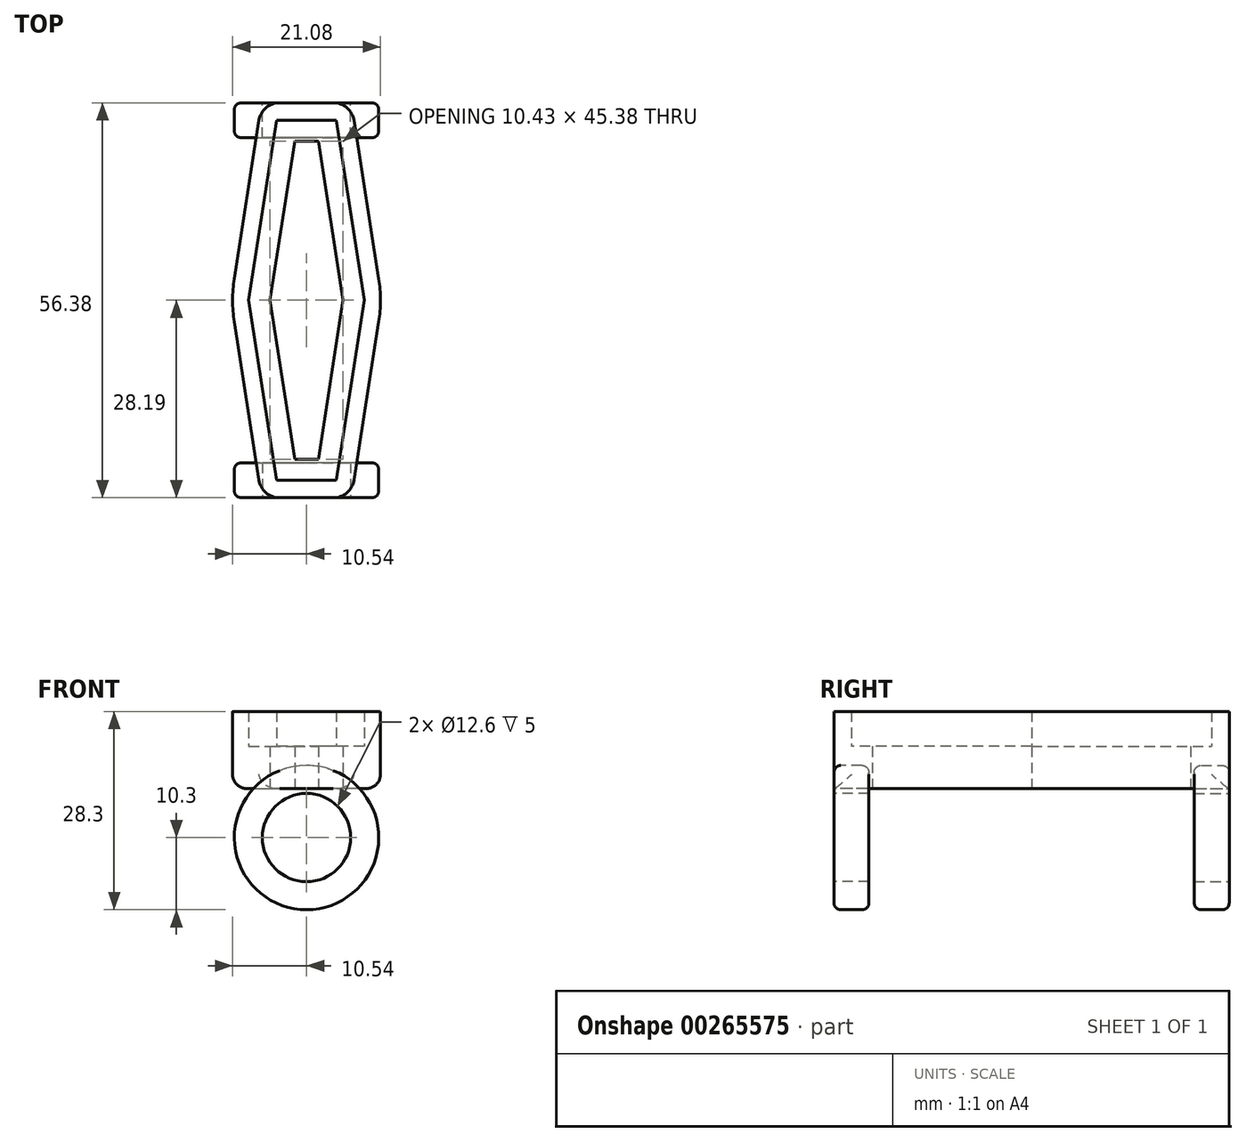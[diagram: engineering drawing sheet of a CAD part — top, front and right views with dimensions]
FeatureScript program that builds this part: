
annotation { "Feature Type Name" : "Feature", "Feature Type Description" : "" }
export const myFeature = defineFeature(function(context is Context, id is Id, definition is map)
    precondition{}
    {
        {
            var Q0;
            Q0=qCreatedBy(makeId("Top.planeOp"),FACE);
            var sketch = newSketch(context, id + "F0", { "sketchPlane" : qUnion([Q0])});
            skLineSegment(sketch, "E0", {"start": v(0, 0) * mm, "end": v(8.25, 0) * mm, "construction": true});
            skLineSegment(sketch, "E1", {"start": v(8.25, 0) * mm, "end": v(4.25, 25.7) * mm});
            skLineSegment(sketch, "E2", {"start": v(0, 0) * mm, "end": v(0, 25.46) * mm, "construction": true});
            skLineSegment(sketch, "E3", {"start": v(4.25, 25.7) * mm, "end": v(0, 25.7) * mm});
            skLineSegment(sketch, "E4.MirrorCS", {"start": v(-4.25, 25.7) * mm, "end": v(0, 25.7) * mm});
            skLineSegment(sketch, "E5.MirrorCS", {"start": v(-8.25, 0) * mm, "end": v(-4.25, 25.7) * mm});
            skLineSegment(sketch, "E6.MirrorCS", {"start": v(0, 0) * mm, "end": v(-8.25, 0) * mm, "construction": true});
            skLineSegment(sketch, "E7.MirrorCS", {"start": v(-8.25, 0) * mm, "end": v(-4.25, -25.7) * mm});
            skLineSegment(sketch, "E8.MirrorCS", {"start": v(-4.25, -25.7) * mm, "end": v(0, -25.7) * mm});
            skLineSegment(sketch, "E9.MirrorCS", {"start": v(4.25, -25.7) * mm, "end": v(0, -25.7) * mm});
            skLineSegment(sketch, "E10.MirrorCS", {"start": v(8.25, 0) * mm, "end": v(4.25, -25.7) * mm});
            skLineSegment(sketch, "E11.0", {"start": v(4.25, 22.7) * mm, "end": v(0, 22.7) * mm});
            skLineSegment(sketch, "E11.1", {"start": v(-4.25, 22.7) * mm, "end": v(0, 22.7) * mm});
            skLineSegment(sketch, "E12.MirrorCS", {"start": v(-4.25, -22.7) * mm, "end": v(0, -22.7) * mm});
            skLineSegment(sketch, "E13.MirrorCS", {"start": v(4.25, -22.7) * mm, "end": v(0, -22.7) * mm});
            skLineSegment(sketch, "E14.0", {"start": v(-10.78, 0) * mm, "end": v(-6.4, -28.2) * mm});
            skLineSegment(sketch, "E14.1", {"start": v(-6.4, -28.2) * mm, "end": v(0, -28.2) * mm});
            skLineSegment(sketch, "E14.2", {"start": v(-10.78, 0) * mm, "end": v(-6.4, 28.2) * mm});
            skLineSegment(sketch, "E14.3", {"start": v(6.4, -28.2) * mm, "end": v(0, -28.2) * mm});
            skLineSegment(sketch, "E14.4", {"start": v(-6.4, 28.2) * mm, "end": v(0, 28.2) * mm});
            skLineSegment(sketch, "E14.5", {"start": v(6.4, 28.2) * mm, "end": v(0, 28.2) * mm});
            skLineSegment(sketch, "E14.6", {"start": v(10.78, 0) * mm, "end": v(6.4, 28.2) * mm});
            skLineSegment(sketch, "E14.7", {"start": v(10.78, 0) * mm, "end": v(6.4, -28.2) * mm});
            skLineSegment(sketch, "E15.0", {"start": v(-5.21, 0) * mm, "end": v(-1.68, -22.7) * mm});
            skLineSegment(sketch, "E15.1", {"start": v(-1.68, -22.7) * mm, "end": v(0, -22.7) * mm});
            skLineSegment(sketch, "E15.2", {"start": v(-5.21, 0) * mm, "end": v(-1.68, 22.7) * mm});
            skLineSegment(sketch, "E15.3", {"start": v(1.68, -22.7) * mm, "end": v(0, -22.7) * mm});
            skLineSegment(sketch, "E15.4", {"start": v(-1.68, 22.7) * mm, "end": v(0, 22.7) * mm});
            skLineSegment(sketch, "E15.5", {"start": v(1.68, 22.7) * mm, "end": v(0, 22.7) * mm});
            skLineSegment(sketch, "E15.6", {"start": v(5.21, 0) * mm, "end": v(1.68, 22.7) * mm});
            skLineSegment(sketch, "E15.7", {"start": v(5.21, 0) * mm, "end": v(1.68, -22.7) * mm});
            skSolve(sketch);
        }
        {
            var Q0;
            {var subQ9=sQuery(id+"F0.wireOp",EDGE,"E5.MirrorCS");Q0=makeQuery(id+"F0.imprint","IMPRINT",FACE,{"disambiguationData":[TD([[makeQuery(id+"F0.imprint","IMPRINT",EDGE,{"derivedFrom":subQ9}),-1.0]])]});}
            var Q1;
            {var subQ3=sQuery(id+"F0.wireOp",EDGE,"E3");var subQ8=sQuery(id+"F0.wireOp",EDGE,"E4.MirrorCS");var subQ10=makeQuery(id+"F0.imprint","INTERSECT",VERTEX,{"derivedFrom":[subQ3,subQ8]});Q1=makeQuery(id+"F0.imprint","IMPRINT",FACE,{"disambiguationData":[TD([[makeQuery(id+"F0.imprint","IMPRINT",EDGE,{"disambiguationData":[TD([[subQ10,1.0]])],"derivedFrom":subQ3}),1.0]])]});}
            var Q2;
            {var subQ5=sQuery(id+"F0.wireOp",EDGE,"E1");Q2=makeQuery(id+"F0.imprint","IMPRINT",FACE,{"disambiguationData":[TD([[makeQuery(id+"F0.imprint","IMPRINT",EDGE,{"derivedFrom":subQ5}),1.0]])]});}
            var Q3;
            {var subQ3=sQuery(id+"F0.wireOp",EDGE,"E9.MirrorCS");var subQ5=sQuery(id+"F0.wireOp",EDGE,"E8.MirrorCS");var subQ6=makeQuery(id+"F0.imprint","INTERSECT",VERTEX,{"derivedFrom":[subQ5,subQ3]});Q3=makeQuery(id+"F0.imprint","IMPRINT",FACE,{"disambiguationData":[TD([[makeQuery(id+"F0.imprint","IMPRINT",EDGE,{"disambiguationData":[TD([[subQ6,1.0]])],"derivedFrom":subQ5}),1.0]])]});}
            extrude(context, id + "F1", {"entities" : qUnion([Q0, Q1, Q2, Q3]), "depth" : 6 * mm});
        }
        {
            var Q0;
            Q0 = qSketchRegion(id + "F0", true);
            extrude(context, id + "F2", {"entities" : qUnion([Q0]), "operationType" : NewBodyOperationType.ADD, "depth" : 11 * mm});
        }
        {
            var Q0;
            Q0=makeQuery(id+"F2.opExtrude","SWEPT_FACE",FACE,{"disambiguationData":[OSD([sQuery(id+"F0.wireOp",EDGE,"E14.1"),sQuery(id+"F0.wireOp",EDGE,"E14.3")])]});
            var sketch = newSketch(context, id + "F3", { "sketchPlane" : qUnion([Q0])});
            skLineSegment(sketch, "E16", {"start": v(0, 0) * mm, "end": v(0, -7) * mm});
            skCircle(sketch, "E17", {"center": v(0, -7) * mm, "radius": 6.3 * mm});
            skCircle(sketch, "E18.0", {"center": v(0, -7) * mm, "radius": 10.3 * mm});
            skSolve(sketch);
        }
        {
            var Q0;
            Q0 = qSketchRegion(id + "F3", true);
            extrude(context, id + "F4", {"entities" : qUnion([Q0]), "oppositeDirection" : true, "depth" : 5 * mm});
        }
        {
            var Q0;
            {var subQ0=sQuery(id+"F0.wireOp",EDGE,"E10.MirrorCS");var subQ1=sQuery(id+"F0.wireOp",EDGE,"E9.MirrorCS");var subQ2=sQuery(id+"F0.wireOp",EDGE,"E8.MirrorCS");var subQ3=sQuery(id+"F0.wireOp",EDGE,"E7.MirrorCS");var subQ4=sQuery(id+"F0.wireOp",EDGE,"E5.MirrorCS");var subQ5=sQuery(id+"F0.wireOp",EDGE,"E4.MirrorCS");var subQ6=sQuery(id+"F0.wireOp",EDGE,"E3");var subQ7=sQuery(id+"F0.wireOp",EDGE,"E1");Q0=makeQuery(id+"F2.boolean.opBoolean","MERGE",FACE,{"derivedFrom":[makeQuery(id+"F1.opExtrude","CAP_FACE",FACE,{"disambiguationData":[OSD([subQ7,subQ6,subQ5,subQ4,subQ3,subQ2,subQ1,subQ0,sQuery(id+"F0.wireOp",EDGE,"E15.0"),sQuery(id+"F0.wireOp",EDGE,"E15.1"),sQuery(id+"F0.wireOp",EDGE,"E15.2"),sQuery(id+"F0.wireOp",EDGE,"E15.3"),sQuery(id+"F0.wireOp",EDGE,"E15.4"),sQuery(id+"F0.wireOp",EDGE,"E15.5"),sQuery(id+"F0.wireOp",EDGE,"E15.6"),sQuery(id+"F0.wireOp",EDGE,"E15.7")])],"isStart":true}),makeQuery(id+"F2.opExtrude","CAP_FACE",FACE,{"disambiguationData":[OSD([subQ7,subQ6,subQ5,subQ4,subQ3,subQ2,subQ1,subQ0,sQuery(id+"F0.wireOp",EDGE,"E14.0"),sQuery(id+"F0.wireOp",EDGE,"E14.1"),sQuery(id+"F0.wireOp",EDGE,"E14.2"),sQuery(id+"F0.wireOp",EDGE,"E14.3"),sQuery(id+"F0.wireOp",EDGE,"E14.4"),sQuery(id+"F0.wireOp",EDGE,"E14.5"),sQuery(id+"F0.wireOp",EDGE,"E14.6"),sQuery(id+"F0.wireOp",EDGE,"E14.7")])],"isStart":true})]});}
            var sketch = newSketch(context, id + "F5", { "sketchPlane" : qUnion([Q0])});
            skLineSegment(sketch, "E19", {"start": v(10.78, 0) * mm, "end": v(-10.78, 0) * mm});
            skSolve(sketch);
        }
        {
            var Q0;
            Q0=sQuery(id+"F5.wireOp",EDGE,"E19");
            extrude(context, id + "F6", {"bodyType" : ToolBodyType.SURFACE, "surfaceEntities" : qUnion([Q0]), "depth" : 25 * mm});
        }
        {
            var Q0;
            Q0=makeQuery(id+"F4.opExtrude","SWEPT_BODY",BODY,{"disambiguationData":[OSD([sQuery(id+"F3.wireOp",EDGE,"E17"),sQuery(id+"F3.wireOp",EDGE,"E18.0")])]});
            var Q1;
            Q1=makeQuery(id+"F6.opExtrude","SWEPT_FACE",FACE,{"disambiguationData":[OSD([sQuery(id+"F5.wireOp",EDGE,"E19")])]});
            mirror(context, id + "F7", {"entities" : qUnion([Q0]), "mirrorPlane" : qUnion([Q1])});
        }
        {
            var Q0;
            Q0=makeQuery(id+"F2.opExtrude","CAP_EDGE",EDGE,{"disambiguationData":[OSD([sQuery(id+"F0.wireOp",EDGE,"E14.0")])],"isStart":true});
            var Q1;
            Q1=makeQuery(id+"F2.opExtrude","CAP_EDGE",EDGE,{"disambiguationData":[OSD([sQuery(id+"F0.wireOp",EDGE,"E14.2")])],"isStart":true});
            var Q2;
            Q2=makeQuery(id+"F2.opExtrude","CAP_EDGE",EDGE,{"disambiguationData":[OSD([sQuery(id+"F0.wireOp",EDGE,"E14.6")])],"isStart":true});
            var Q3;
            Q3=makeQuery(id+"F2.opExtrude","CAP_EDGE",EDGE,{"disambiguationData":[OSD([sQuery(id+"F0.wireOp",EDGE,"E14.7")])],"isStart":true});
            fillet(context, id + "F8", {"entities" : qUnion([Q0, Q1, Q2, Q3]), "radius" : 2 * mm, "tangentPropagation" : true, "allowEdgeOverflow" : false});
        }
        {
            var Q0;
            Q0=makeQuery(id+"F4.opExtrude","CAP_EDGE",EDGE,{"disambiguationData":[OSD([sQuery(id+"F3.wireOp",EDGE,"E18.0")])],"isStart":true});
            var Q1;
            Q1=makeQuery(id+"F7.opPattern","COPY",EDGE,{"derivedFrom":makeQuery(id+"F4.opExtrude","CAP_EDGE",EDGE,{"disambiguationData":[OSD([sQuery(id+"F3.wireOp",EDGE,"E18.0")])],"isStart":true}),"instanceName":"1"});
            var Q2;
            Q2=makeQuery(id+"F4.opExtrude","CAP_EDGE",EDGE,{"disambiguationData":[OSD([sQuery(id+"F3.wireOp",EDGE,"E18.0")])],"isStart":false});
            var Q3;
            Q3=makeQuery(id+"F7.opPattern","COPY",EDGE,{"derivedFrom":makeQuery(id+"F4.opExtrude","CAP_EDGE",EDGE,{"disambiguationData":[OSD([sQuery(id+"F3.wireOp",EDGE,"E18.0")])],"isStart":false}),"instanceName":"1"});
            fillet(context, id + "F9", {"entities" : qUnion([Q0, Q1, Q2, Q3]), "radius" : 1 * mm, "tangentPropagation" : true, "allowEdgeOverflow" : false});
        }
        {
            var Q0;
            Q0=makeQuery(id+"F2.opExtrude","SWEPT_EDGE",EDGE,{"disambiguationData":[OSD([sQuery(id+"F0.wireOp",EDGE,"E14.0"),sQuery(id+"F0.wireOp",EDGE,"E14.1")])]});
            var Q1;
            Q1=makeQuery(id+"F2.opExtrude","SWEPT_EDGE",EDGE,{"disambiguationData":[OSD([sQuery(id+"F0.wireOp",EDGE,"E14.3"),sQuery(id+"F0.wireOp",EDGE,"E14.7")])]});
            var Q2;
            Q2=makeQuery(id+"F2.opExtrude","SWEPT_EDGE",EDGE,{"disambiguationData":[OSD([sQuery(id+"F0.wireOp",EDGE,"E14.2"),sQuery(id+"F0.wireOp",EDGE,"E14.4")])]});
            var Q3;
            Q3=makeQuery(id+"F2.opExtrude","SWEPT_EDGE",EDGE,{"disambiguationData":[OSD([sQuery(id+"F0.wireOp",EDGE,"E14.5"),sQuery(id+"F0.wireOp",EDGE,"E14.6")])]});
            fillet(context, id + "F10", {"entities" : qUnion([Q0, Q1, Q2, Q3]), "radius" : 3 * mm, "allowEdgeOverflow" : false});
        }
        {
            var Q0;
            Q0=makeQuery(id+"F2.opExtrude","SWEPT_EDGE",EDGE,{"disambiguationData":[OSD([sQuery(id+"F0.wireOp",EDGE,"E14.0"),sQuery(id+"F0.wireOp",EDGE,"E14.2")])]});
            var Q1;
            Q1=makeQuery(id+"F2.opExtrude","SWEPT_EDGE",EDGE,{"disambiguationData":[OSD([sQuery(id+"F0.wireOp",EDGE,"E14.6"),sQuery(id+"F0.wireOp",EDGE,"E14.7")])]});
            fillet(context, id + "F11", {"entities" : qUnion([Q0, Q1]), "radius" : 20 * mm, "tangentPropagation" : true, "allowEdgeOverflow" : false});
        }
    });
